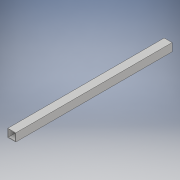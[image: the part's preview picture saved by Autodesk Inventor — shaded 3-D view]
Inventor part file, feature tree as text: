
AUTODESK INVENTOR PART (.ipt)
format: ipt  version: 2019.3 (Build 233278000, 278)  size: 101,888 bytes
history: native  units: mm
features: other x3, reference x2, extrude x1, sketch x1
ambient origin geometry x8: Origin, YZ Plane, XZ Plane, XY Plane, X Axis, Y Axis, Z Axis, Center Point
bodies: Solid1 (feature_tree)
feature tree (7):
  extrude  "Extrusion1"  Depth=22.225mm
  sketch  "Sketch1"  dims[d0=22.225mm d1=22.225mm d3=1.5875mm d8=500.0mm d9=0.0mm]
  reference  "Reference1"
  reference  "Reference2"
  parser-record x1  (decoder bookkeeping rows leaked as tree rows — omitted from the tree; the rows remain in map.json)
  other  "Assembly.iam"
  other  "RailMount:1"
note: 1 file-system path scrubbed to <path> (originals preserved in map.json)
